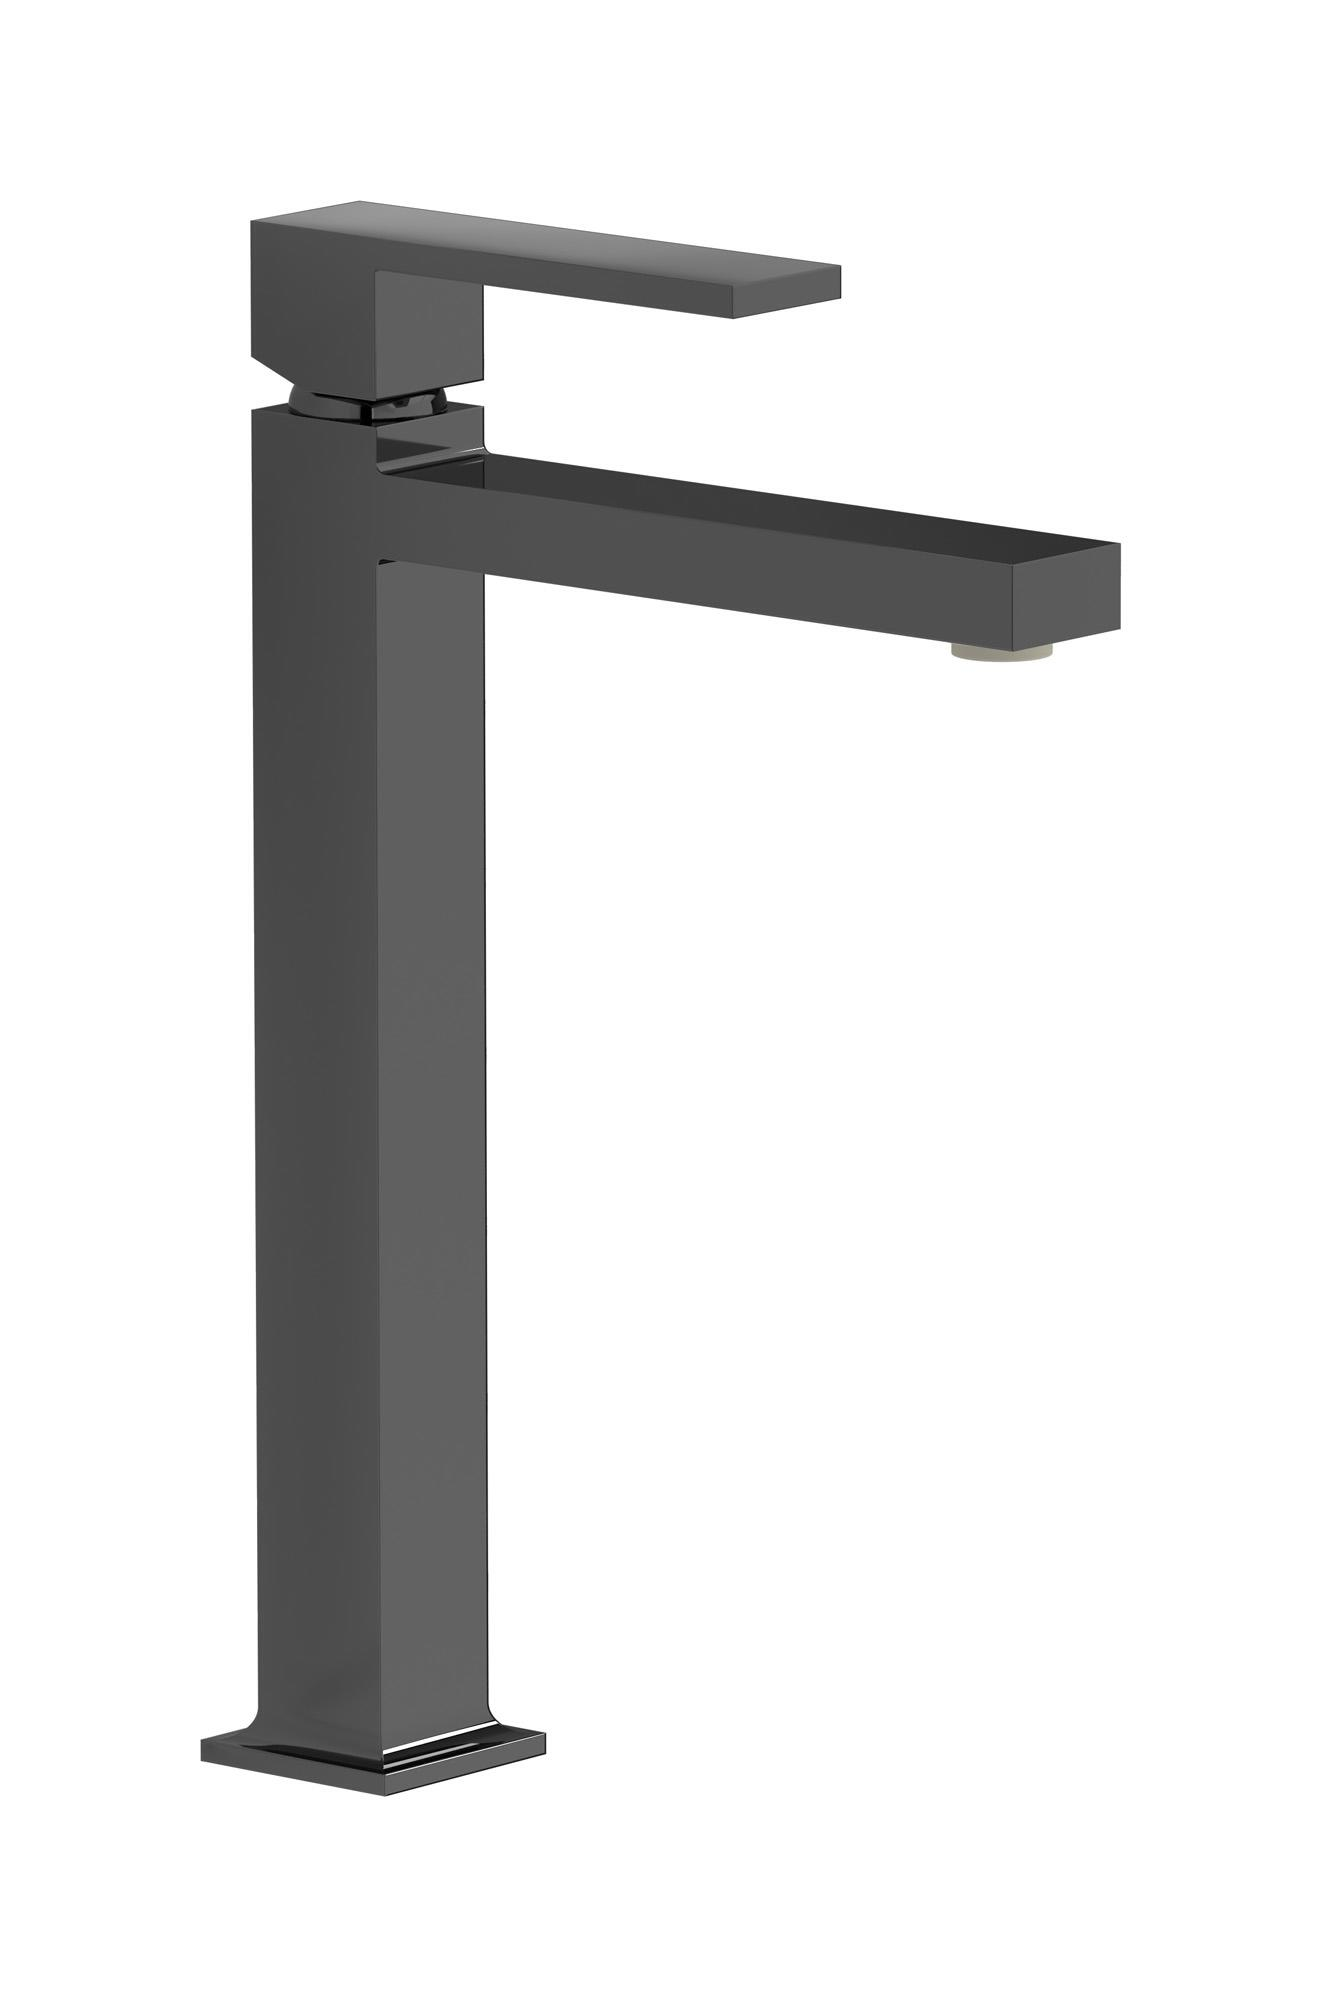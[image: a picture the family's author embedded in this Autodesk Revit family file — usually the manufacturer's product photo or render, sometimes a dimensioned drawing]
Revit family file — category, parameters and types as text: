
# Revit family: RU203
name_source: partatom
category: Apparecchi idraulici
units: mm (PartAtom-declared; Revit-internal decimal feet)

## family parameters
Basato su piano di lavoro = No
Condiviso = No
Mantieni orientamento annotazione = No
Numero OmniClass = 23.45.55.17
Punto di calcolo locali = No
Quota connettore circolare = Usa diametro
Sempre verticale = Sì
Taglio con vuoti quando caricato = No
Tipo di parte = Normale
Titolo OmniClass = Mixing Faucets

## types (12) — shared parameters
Cold water inlet = 10 mm  [stored 0.0328084 ft]
Commenti sul tipo = Tall mini monohole washbasin mixer complete with drain
Connessione CW = No
Connessione HW = No
Connessione di scarico = No
Connessione di ventilazione = No
Descrizione = Tall mini monohole washbasin mixer complete with drain
Hot water inlet = 10 mm  [stored 0.0328084 ft]
Produttore = IB Rubinetterie S.p.A.
URL = https://www.weareib.it
zero-valued in all types: Prospetto di default

## per-type parameters (varying)
| type | Finishes surface | Immagine tipo | Modello |
| Chrome | IB_Chrome | RU203CC.jpg | RU203CC |
| Matt White | IB_matt white | RU203BO.jpg | RU203BO |
| Black Chrome | IB_Black chrome | RU203CF.jpg | RU203CF |
| Brushed Black Chrome | IB_Brushed black chrome | RU203CS.jpg | RU203CS |
| Pale Gold | IB_Pale gold | RU203II.jpg | RU203II |
| Brushed Pale Gold | IB_brushed pale gold | RU203IS.jpg | RU203IS |
| Matt Black | IB_matt black | RU203NP.jpg | RU203NP |
| Gold | IB_gold | RU203OO.jpg | RU203OO |
| Brushed Gold | IB_brushed gold | RU203OS.jpg | RU203OS |
| Rose Gold | IB_Rose gold | RU203RS.jpg | RU203RS |
| Brushed Rose Gold | IB_Brushed rose gold | RU203SR.jpg | RU203SR |
| Brushed Nickel | IB_Brushed nickel | RU203SS.jpg | RU203SS |

note: [stored X ft] marks values corroborated as IEEE doubles in the binary element streams (Revit-internal decimal feet)
